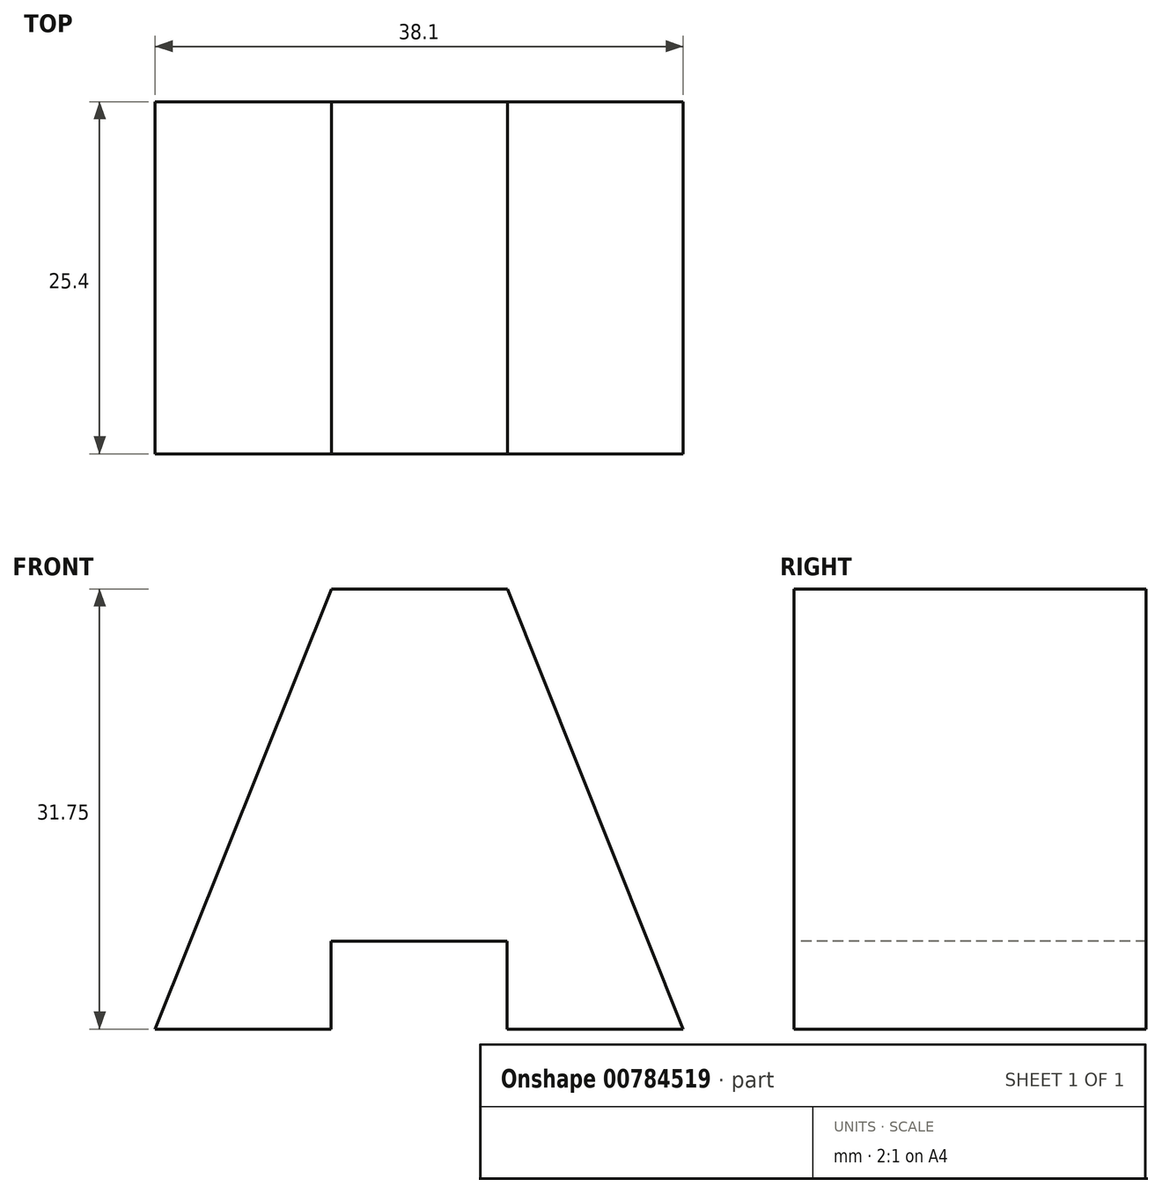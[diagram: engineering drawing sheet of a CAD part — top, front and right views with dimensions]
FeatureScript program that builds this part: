
annotation { "Feature Type Name" : "Feature", "Feature Type Description" : "" }
export const myFeature = defineFeature(function(context is Context, id is Id, definition is map)
    precondition{}
    {
        {
            var Q0;
            Q0=qCreatedBy(makeId("Front.planeOp"),FACE);
            var sketch = newSketch(context, id + "F0", { "sketchPlane" : qUnion([Q0])});
            skLineSegment(sketch, "E0", {"start": v(0, 0) * mm, "end": v(38.1, 0) * mm});
            skLineSegment(sketch, "E1", {"start": v(38.1, 0) * mm, "end": v(38.1, 31.75) * mm});
            skLineSegment(sketch, "E2", {"start": v(38.1, 31.75) * mm, "end": v(0, 31.75) * mm});
            skLineSegment(sketch, "E3", {"start": v(0, 31.75) * mm, "end": v(0, 0) * mm});
            skSolve(sketch);
        }
        {
            var Q0;
            Q0 = qSketchRegion(id + "F0", true);
            extrude(context, id + "F1", {"entities" : qUnion([Q0]), "depth" : 25.4 * mm, "offsetDistance" : 25.4 * mm});
        }
        {
            var Q0;
            Q0=makeQuery(id+"F1.opExtrude","CAP_FACE",FACE,{"disambiguationData":[OSD([sQuery(id+"F0.wireOp",EDGE,"E0"),sQuery(id+"F0.wireOp",EDGE,"E1"),sQuery(id+"F0.wireOp",EDGE,"E2"),sQuery(id+"F0.wireOp",EDGE,"E3")])],"isStart":false});
            var sketch = newSketch(context, id + "F2", { "sketchPlane" : qUnion([Q0])});
            skLineSegment(sketch, "E4", {"start": v(0, 0) * mm, "end": v(12.7, 0) * mm});
            skLineSegment(sketch, "E5", {"start": v(12.7, 0) * mm, "end": v(12.7, 6.35) * mm});
            skLineSegment(sketch, "E6", {"start": v(12.7, 6.35) * mm, "end": v(25.4, 6.35) * mm});
            skLineSegment(sketch, "E7", {"start": v(25.4, 6.35) * mm, "end": v(25.4, 0) * mm});
            skSolve(sketch);
        }
        {
            var Q0;
            {var subQ0=sQuery(id+"F2.wireOp",EDGE,"E5");Q0=makeQuery(id+"F2.imprint","IMPRINT",FACE,{"disambiguationData":[TD([[makeQuery(id+"F2.imprint","IMPRINT",EDGE,{"derivedFrom":subQ0}),-1.0]])]});}
            extrude(context, id + "F3", {"entities" : qUnion([Q0]), "operationType" : NewBodyOperationType.REMOVE, "oppositeDirection" : true, "depth" : 25.4 * mm, "offsetDistance" : 25.4 * mm});
        }
        {
            var Q0;
            Q0=makeQuery(id+"F1.opExtrude","CAP_FACE",FACE,{"disambiguationData":[OSD([sQuery(id+"F0.wireOp",EDGE,"E0"),sQuery(id+"F0.wireOp",EDGE,"E1"),sQuery(id+"F0.wireOp",EDGE,"E2"),sQuery(id+"F0.wireOp",EDGE,"E3")])],"isStart":false});
            var sketch = newSketch(context, id + "F4", { "sketchPlane" : qUnion([Q0])});
            skLineSegment(sketch, "E8", {"start": v(0, 0) * mm, "end": v(12.72, 31.75) * mm});
            skLineSegment(sketch, "E9", {"start": v(12.72, 31.75) * mm, "end": v(25.42, 31.75) * mm});
            skLineSegment(sketch, "E10", {"start": v(25.42, 31.75) * mm, "end": v(38.1, 0) * mm});
            skSolve(sketch);
        }
        {
            var Q0;
            {var subQ0=sQuery(id+"F4.wireOp",EDGE,"E10");Q0=makeQuery(id+"F4.imprint","IMPRINT",FACE,{"disambiguationData":[TD([[makeQuery(id+"F4.imprint","IMPRINT",EDGE,{"derivedFrom":subQ0}),1.0]])]});}
            var Q1;
            {var subQ0=sQuery(id+"F4.wireOp",EDGE,"E8");Q1=makeQuery(id+"F4.imprint","IMPRINT",FACE,{"disambiguationData":[TD([[makeQuery(id+"F4.imprint","IMPRINT",EDGE,{"derivedFrom":subQ0}),1.0]])]});}
            extrude(context, id + "F5", {"entities" : qUnion([Q0, Q1]), "operationType" : NewBodyOperationType.REMOVE, "oppositeDirection" : true, "depth" : 25.4 * mm, "offsetDistance" : 25.4 * mm});
        }
    });
